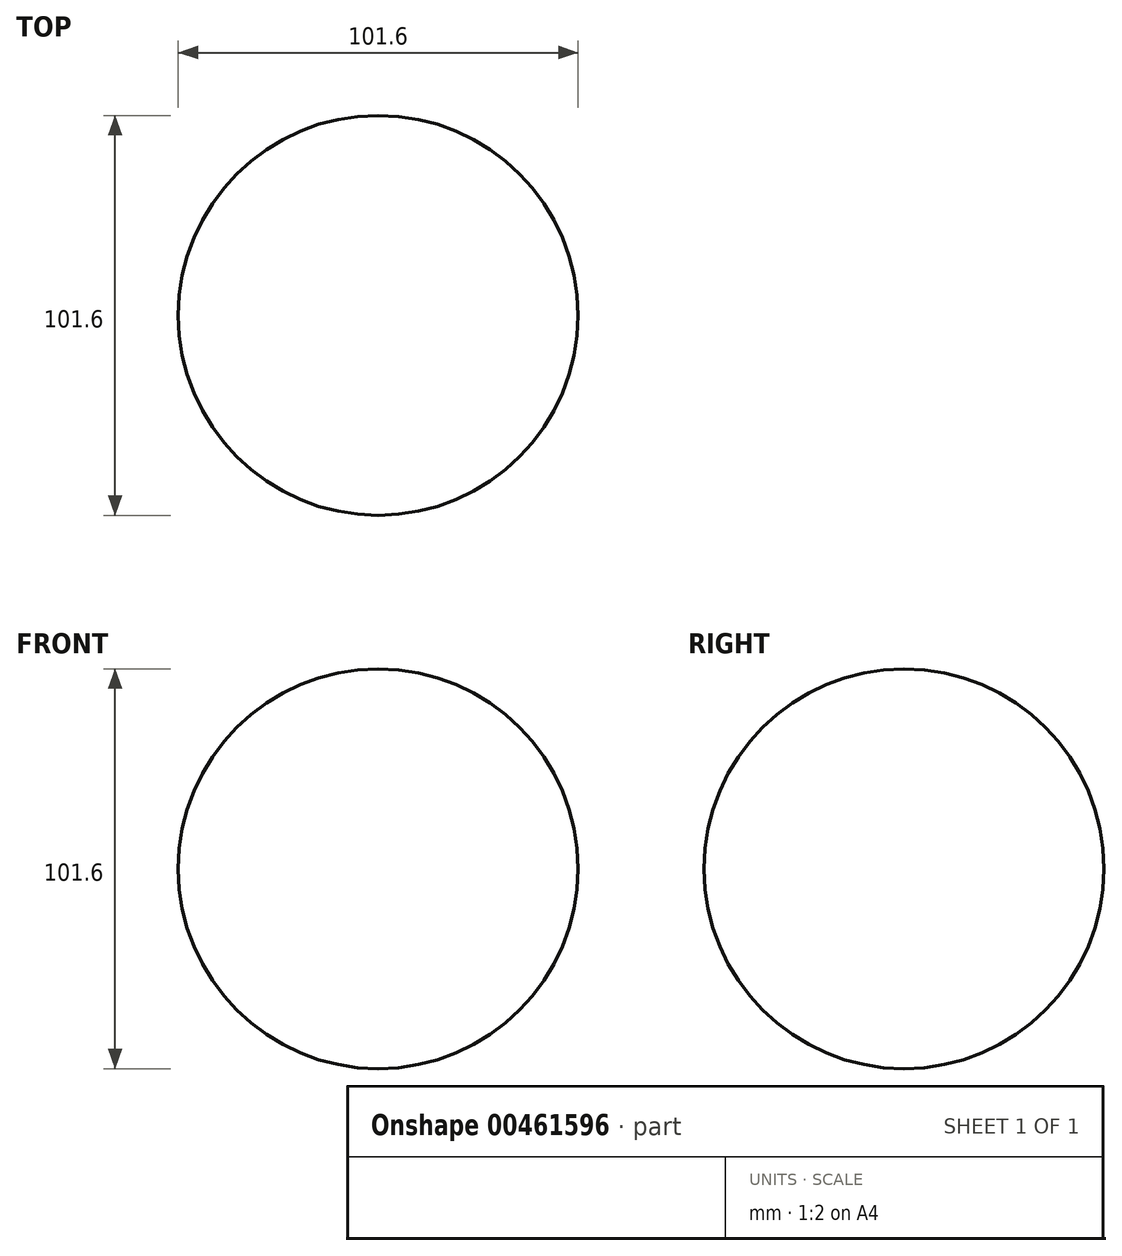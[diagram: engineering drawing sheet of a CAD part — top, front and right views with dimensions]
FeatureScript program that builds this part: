
annotation { "Feature Type Name" : "Feature", "Feature Type Description" : "" }
export const myFeature = defineFeature(function(context is Context, id is Id, definition is map)
    precondition{}
    {
        {
            var Q0;
            Q0=qCreatedBy(makeId("Top.planeOp"),FACE);
            var sketch = newSketch(context, id + "F0", { "sketchPlane" : qUnion([Q0])});
            skCircle(sketch, "E0", {"center": v(0, 0) * mm, "radius": 50.8 * mm});
            skLineSegment(sketch, "E1", {"start": v(0, 50.8) * mm, "end": v(0, -50.8) * mm});
            skSolve(sketch);
        }
        {
            var Q0;
            {var subQ0=sQuery(id+"F0.wireOp",EDGE,"E1");Q0=makeQuery(id+"F0.imprint","IMPRINT",FACE,{"disambiguationData":[TD([[makeQuery(id+"F0.imprint","IMPRINT",EDGE,{"derivedFrom":subQ0}),-1.0]])]});}
            var Q1;
            Q1=sQuery(id+"F0.wireOp",EDGE,"E1");
            revolve(context, id + "F1", {"entities" : qUnion([Q0]), "axis" : qUnion([Q1]), "revolveType" : RevolveType.FULL});
        }
    });
